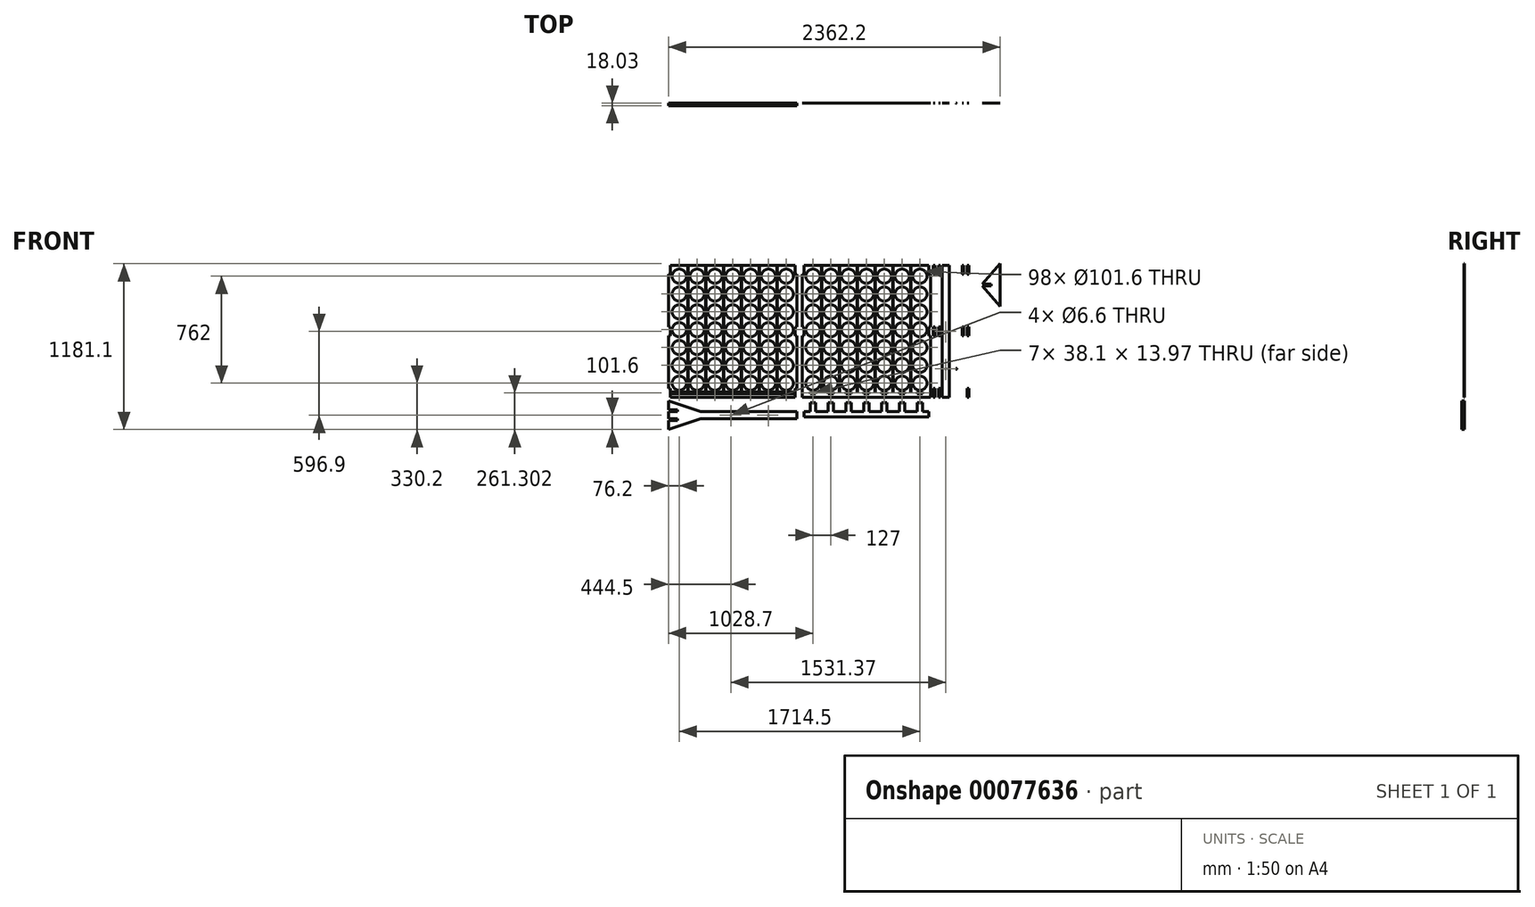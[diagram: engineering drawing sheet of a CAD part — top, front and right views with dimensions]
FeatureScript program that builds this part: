
annotation { "Feature Type Name" : "Feature", "Feature Type Description" : "" }
export const myFeature = defineFeature(function(context is Context, id is Id, definition is map)
    precondition{}
    {
        {
            assignVariable(context, id + "F0", {"name" : "Thickness", "anyValue" : .48});
        }
        {
            var Q0;
            Q0=qCreatedBy(makeId("Front.planeOp"),FACE);
            var sketch = newSketch(context, id + "F1", { "sketchPlane" : qUnion([Q0])});
            skLineSegment(sketch, "E0.bottom", {"start": v(-1219.2, 609.6) * mm, "end": v(1219.2, 609.6) * mm});
            skLineSegment(sketch, "E0.top", {"start": v(-1219.2, -609.6) * mm, "end": v(1219.2, -609.6) * mm});
            skLineSegment(sketch, "E0.left", {"start": v(-1219.2, 609.6) * mm, "end": v(-1219.2, -609.6) * mm});
            skLineSegment(sketch, "E0.right", {"start": v(1219.2, 609.6) * mm, "end": v(1219.2, -609.6) * mm});
            skPoint(sketch, "E0.middle", {"position": v(0, 0) * mm});
            skLineSegment(sketch, "E1.bottom", {"start": v(-1181.1, 571.5) * mm, "end": v(-266.7, 571.5) * mm});
            skLineSegment(sketch, "E1.top", {"start": v(-1181.1, -368.3) * mm, "end": v(-266.7, -368.3) * mm});
            skLineSegment(sketch, "E1.left", {"start": v(-1181.1, 571.5) * mm, "end": v(-1181.1, -368.3) * mm});
            skLineSegment(sketch, "E1.right", {"start": v(-266.7, 571.5) * mm, "end": v(-266.7, -368.3) * mm});
            skLineSegment(sketch, "E2.bottom", {"start": v(-228.6, 571.5) * mm, "end": v(685.8, 571.5) * mm});
            skLineSegment(sketch, "E2.top", {"start": v(-228.6, -368.3) * mm, "end": v(685.8, -368.3) * mm});
            skLineSegment(sketch, "E2.left", {"start": v(-228.6, 571.5) * mm, "end": v(-228.6, -368.3) * mm});
            skLineSegment(sketch, "E2.right", {"start": v(685.8, 571.5) * mm, "end": v(685.8, -368.3) * mm});
            skCircle(sketch, "E3", {"center": v(-1104.9, 495.3) * mm, "radius": 50.8 * mm});
            skCircle(sketch, "E4.0.1.0", {"center": v(-1104.9, 368.3) * mm, "radius": 50.8 * mm});
            skCircle(sketch, "E4.0.2.0", {"center": v(-1104.9, 241.3) * mm, "radius": 50.8 * mm});
            skCircle(sketch, "E4.0.3.0", {"center": v(-1104.9, 114.3) * mm, "radius": 50.8 * mm});
            skCircle(sketch, "E4.0.4.0", {"center": v(-1104.9, -12.7) * mm, "radius": 50.8 * mm});
            skCircle(sketch, "E4.0.5.0", {"center": v(-1104.9, -139.7) * mm, "radius": 50.8 * mm});
            skCircle(sketch, "E4.1.0.0", {"center": v(-977.9, 495.3) * mm, "radius": 50.8 * mm});
            skCircle(sketch, "E4.1.1.0", {"center": v(-977.9, 368.3) * mm, "radius": 50.8 * mm});
            skCircle(sketch, "E4.1.2.0", {"center": v(-977.9, 241.3) * mm, "radius": 50.8 * mm});
            skCircle(sketch, "E4.1.3.0", {"center": v(-977.9, 114.3) * mm, "radius": 50.8 * mm});
            skCircle(sketch, "E4.1.4.0", {"center": v(-977.9, -12.7) * mm, "radius": 50.8 * mm});
            skCircle(sketch, "E4.1.5.0", {"center": v(-977.9, -139.7) * mm, "radius": 50.8 * mm});
            skCircle(sketch, "E4.2.0.0", {"center": v(-850.9, 495.3) * mm, "radius": 50.8 * mm});
            skCircle(sketch, "E4.2.1.0", {"center": v(-850.9, 368.3) * mm, "radius": 50.8 * mm});
            skCircle(sketch, "E4.2.2.0", {"center": v(-850.9, 241.3) * mm, "radius": 50.8 * mm});
            skCircle(sketch, "E4.2.3.0", {"center": v(-850.9, 114.3) * mm, "radius": 50.8 * mm});
            skCircle(sketch, "E4.2.4.0", {"center": v(-850.9, -12.7) * mm, "radius": 50.8 * mm});
            skCircle(sketch, "E4.2.5.0", {"center": v(-850.9, -139.7) * mm, "radius": 50.8 * mm});
            skCircle(sketch, "E4.3.0.0", {"center": v(-723.9, 495.3) * mm, "radius": 50.8 * mm});
            skCircle(sketch, "E4.3.1.0", {"center": v(-723.9, 368.3) * mm, "radius": 50.8 * mm});
            skCircle(sketch, "E4.3.2.0", {"center": v(-723.9, 241.3) * mm, "radius": 50.8 * mm});
            skCircle(sketch, "E4.3.3.0", {"center": v(-723.9, 114.3) * mm, "radius": 50.8 * mm});
            skCircle(sketch, "E4.3.4.0", {"center": v(-723.9, -12.7) * mm, "radius": 50.8 * mm});
            skCircle(sketch, "E4.3.5.0", {"center": v(-723.9, -139.7) * mm, "radius": 50.8 * mm});
            skCircle(sketch, "E4.4.0.0", {"center": v(-596.9, 495.3) * mm, "radius": 50.8 * mm});
            skCircle(sketch, "E4.4.1.0", {"center": v(-596.9, 368.3) * mm, "radius": 50.8 * mm});
            skCircle(sketch, "E4.4.2.0", {"center": v(-596.9, 241.3) * mm, "radius": 50.8 * mm});
            skCircle(sketch, "E4.4.3.0", {"center": v(-596.9, 114.3) * mm, "radius": 50.8 * mm});
            skCircle(sketch, "E4.4.4.0", {"center": v(-596.9, -12.7) * mm, "radius": 50.8 * mm});
            skCircle(sketch, "E4.4.5.0", {"center": v(-596.9, -139.7) * mm, "radius": 50.8 * mm});
            skCircle(sketch, "E4.5.0.0", {"center": v(-469.9, 495.3) * mm, "radius": 50.8 * mm});
            skCircle(sketch, "E4.5.1.0", {"center": v(-469.9, 368.3) * mm, "radius": 50.8 * mm});
            skCircle(sketch, "E4.5.2.0", {"center": v(-469.9, 241.3) * mm, "radius": 50.8 * mm});
            skCircle(sketch, "E4.5.3.0", {"center": v(-469.9, 114.3) * mm, "radius": 50.8 * mm});
            skCircle(sketch, "E4.5.4.0", {"center": v(-469.9, -12.7) * mm, "radius": 50.8 * mm});
            skCircle(sketch, "E4.5.5.0", {"center": v(-469.9, -139.7) * mm, "radius": 50.8 * mm});
            skLineSegment(sketch, "E4.direction1", {"start": v(-1104.9, 495.3) * mm, "end": v(-977.9, 495.3) * mm, "construction": true});
            skLineSegment(sketch, "E4.direction2", {"start": v(-1104.9, 495.3) * mm, "end": v(-1104.9, 368.3) * mm, "construction": true});
            skCircle(sketch, "E5", {"center": v(-152.4, 495.3) * mm, "radius": 50.8 * mm});
            skCircle(sketch, "E6.0.1.0", {"center": v(-152.4, 368.3) * mm, "radius": 50.8 * mm});
            skCircle(sketch, "E6.0.2.0", {"center": v(-152.4, 241.3) * mm, "radius": 50.8 * mm});
            skCircle(sketch, "E6.0.3.0", {"center": v(-152.4, 114.3) * mm, "radius": 50.8 * mm});
            skCircle(sketch, "E6.0.4.0", {"center": v(-152.4, -12.7) * mm, "radius": 50.8 * mm});
            skCircle(sketch, "E6.0.5.0", {"center": v(-152.4, -139.7) * mm, "radius": 50.8 * mm});
            skCircle(sketch, "E6.1.0.0", {"center": v(-25.4, 495.3) * mm, "radius": 50.8 * mm});
            skCircle(sketch, "E6.1.1.0", {"center": v(-25.4, 368.3) * mm, "radius": 50.8 * mm});
            skCircle(sketch, "E6.1.2.0", {"center": v(-25.4, 241.3) * mm, "radius": 50.8 * mm});
            skCircle(sketch, "E6.1.3.0", {"center": v(-25.4, 114.3) * mm, "radius": 50.8 * mm});
            skCircle(sketch, "E6.1.4.0", {"center": v(-25.4, -12.7) * mm, "radius": 50.8 * mm});
            skCircle(sketch, "E6.1.5.0", {"center": v(-25.4, -139.7) * mm, "radius": 50.8 * mm});
            skCircle(sketch, "E6.2.0.0", {"center": v(101.6, 495.3) * mm, "radius": 50.8 * mm});
            skCircle(sketch, "E6.2.1.0", {"center": v(101.6, 368.3) * mm, "radius": 50.8 * mm});
            skCircle(sketch, "E6.2.2.0", {"center": v(101.6, 241.3) * mm, "radius": 50.8 * mm});
            skCircle(sketch, "E6.2.3.0", {"center": v(101.6, 114.3) * mm, "radius": 50.8 * mm});
            skCircle(sketch, "E6.2.4.0", {"center": v(101.6, -12.7) * mm, "radius": 50.8 * mm});
            skCircle(sketch, "E6.2.5.0", {"center": v(101.6, -139.7) * mm, "radius": 50.8 * mm});
            skCircle(sketch, "E6.3.0.0", {"center": v(228.6, 495.3) * mm, "radius": 50.8 * mm});
            skCircle(sketch, "E6.3.1.0", {"center": v(228.6, 368.3) * mm, "radius": 50.8 * mm});
            skCircle(sketch, "E6.3.2.0", {"center": v(228.6, 241.3) * mm, "radius": 50.8 * mm});
            skCircle(sketch, "E6.3.3.0", {"center": v(228.6, 114.3) * mm, "radius": 50.8 * mm});
            skCircle(sketch, "E6.3.4.0", {"center": v(228.6, -12.7) * mm, "radius": 50.8 * mm});
            skCircle(sketch, "E6.3.5.0", {"center": v(228.6, -139.7) * mm, "radius": 50.8 * mm});
            skCircle(sketch, "E6.4.0.0", {"center": v(355.6, 495.3) * mm, "radius": 50.8 * mm});
            skCircle(sketch, "E6.4.1.0", {"center": v(355.6, 368.3) * mm, "radius": 50.8 * mm});
            skCircle(sketch, "E6.4.2.0", {"center": v(355.6, 241.3) * mm, "radius": 50.8 * mm});
            skCircle(sketch, "E6.4.3.0", {"center": v(355.6, 114.3) * mm, "radius": 50.8 * mm});
            skCircle(sketch, "E6.4.4.0", {"center": v(355.6, -12.7) * mm, "radius": 50.8 * mm});
            skCircle(sketch, "E6.4.5.0", {"center": v(355.6, -139.7) * mm, "radius": 50.8 * mm});
            skCircle(sketch, "E6.5.0.0", {"center": v(482.6, 495.3) * mm, "radius": 50.8 * mm});
            skCircle(sketch, "E6.5.1.0", {"center": v(482.6, 368.3) * mm, "radius": 50.8 * mm});
            skCircle(sketch, "E6.5.2.0", {"center": v(482.6, 241.3) * mm, "radius": 50.8 * mm});
            skCircle(sketch, "E6.5.3.0", {"center": v(482.6, 114.3) * mm, "radius": 50.8 * mm});
            skCircle(sketch, "E6.5.4.0", {"center": v(482.6, -12.7) * mm, "radius": 50.8 * mm});
            skCircle(sketch, "E6.5.5.0", {"center": v(482.6, -139.7) * mm, "radius": 50.8 * mm});
            skLineSegment(sketch, "E6.direction1", {"start": v(-152.4, 495.3) * mm, "end": v(-25.4, 495.3) * mm, "construction": true});
            skLineSegment(sketch, "E6.direction2", {"start": v(-152.4, 495.3) * mm, "end": v(-152.4, 368.3) * mm, "construction": true});
            skLineSegment(sketch, "E7", {"start": v(-1041.4, 571.5) * mm, "end": v(-1041.4, -368.3) * mm, "construction": true});
            skPoint(sketch, "E7.startSnap0", {"position": v(-1041.4, 495.3) * mm});
            skLineSegment(sketch, "E8.0", {"start": v(-1042.99, 571.5) * mm, "end": v(-1042.99, -328.61) * mm});
            skLineSegment(sketch, "E9.0", {"start": v(-1039.81, 571.5) * mm, "end": v(-1039.81, -328.61) * mm});
            skLineSegment(sketch, "E10.1.0.0", {"start": v(-912.81, 571.5) * mm, "end": v(-912.81, -328.61) * mm});
            skLineSegment(sketch, "E10.1.0.1", {"start": v(-915.99, 571.5) * mm, "end": v(-915.99, -328.61) * mm});
            skLineSegment(sketch, "E10.2.0.0", {"start": v(-785.81, 571.5) * mm, "end": v(-785.81, -328.61) * mm});
            skLineSegment(sketch, "E10.2.0.1", {"start": v(-788.99, 571.5) * mm, "end": v(-788.99, -328.61) * mm});
            skLineSegment(sketch, "E10.3.0.0", {"start": v(-658.81, 571.5) * mm, "end": v(-658.81, -328.61) * mm});
            skLineSegment(sketch, "E10.3.0.1", {"start": v(-661.99, 571.5) * mm, "end": v(-661.99, -328.61) * mm});
            skLineSegment(sketch, "E10.4.0.0", {"start": v(-531.81, 571.5) * mm, "end": v(-531.81, -328.61) * mm});
            skLineSegment(sketch, "E10.4.0.1", {"start": v(-534.99, 571.5) * mm, "end": v(-534.99, -328.61) * mm});
            skLineSegment(sketch, "E10.direction1", {"start": v(-1039.81, -328.61) * mm, "end": v(-912.81, -328.61) * mm, "construction": true});
            skLineSegment(sketch, "E11", {"start": v(-88.9, 571.5) * mm, "end": v(-88.9, -368.3) * mm, "construction": true});
            skPoint(sketch, "E11.startSnap0", {"position": v(-88.9, 495.3) * mm});
            skLineSegment(sketch, "E12.0", {"start": v(-87.31, 571.5) * mm, "end": v(-87.31, -328.61) * mm});
            skLineSegment(sketch, "E13.0", {"start": v(-90.49, 571.5) * mm, "end": v(-90.49, -328.61) * mm});
            skLineSegment(sketch, "E14.1.0.0", {"start": v(39.69, 571.5) * mm, "end": v(39.69, -328.61) * mm});
            skLineSegment(sketch, "E14.1.0.1", {"start": v(36.51, 571.5) * mm, "end": v(36.51, -328.61) * mm});
            skLineSegment(sketch, "E14.2.0.0", {"start": v(166.69, 571.5) * mm, "end": v(166.69, -328.61) * mm});
            skLineSegment(sketch, "E14.2.0.1", {"start": v(163.51, 571.5) * mm, "end": v(163.51, -328.61) * mm});
            skLineSegment(sketch, "E14.3.0.0", {"start": v(293.69, 571.5) * mm, "end": v(293.69, -328.61) * mm});
            skLineSegment(sketch, "E14.3.0.1", {"start": v(290.51, 571.5) * mm, "end": v(290.51, -328.61) * mm});
            skLineSegment(sketch, "E14.4.0.0", {"start": v(420.69, 571.5) * mm, "end": v(420.69, -328.61) * mm});
            skLineSegment(sketch, "E14.4.0.1", {"start": v(417.51, 571.5) * mm, "end": v(417.51, -328.61) * mm});
            skLineSegment(sketch, "E14.direction1", {"start": v(-87.31, -328.61) * mm, "end": v(39.69, -328.61) * mm, "construction": true});
            skCircle(sketch, "E15.0.6.0", {"center": v(-342.9, 495.3) * mm, "radius": 50.8 * mm});
            skCircle(sketch, "E15.0.6.1", {"center": v(-342.9, 368.3) * mm, "radius": 50.8 * mm});
            skCircle(sketch, "E15.0.6.2", {"center": v(-342.9, 241.3) * mm, "radius": 50.8 * mm});
            skCircle(sketch, "E15.0.6.3", {"center": v(-342.9, 114.3) * mm, "radius": 50.8 * mm});
            skCircle(sketch, "E15.0.6.4", {"center": v(-342.9, -12.7) * mm, "radius": 50.8 * mm});
            skCircle(sketch, "E15.0.6.5", {"center": v(-342.9, -139.7) * mm, "radius": 50.8 * mm});
            skCircle(sketch, "E16.0.0.6", {"center": v(-1104.9, -266.7) * mm, "radius": 50.8 * mm});
            skCircle(sketch, "E16.0.1.6", {"center": v(-977.9, -266.7) * mm, "radius": 50.8 * mm});
            skCircle(sketch, "E16.0.2.6", {"center": v(-850.9, -266.7) * mm, "radius": 50.8 * mm});
            skCircle(sketch, "E16.0.3.6", {"center": v(-723.9, -266.7) * mm, "radius": 50.8 * mm});
            skCircle(sketch, "E16.0.4.6", {"center": v(-596.9, -266.7) * mm, "radius": 50.8 * mm});
            skCircle(sketch, "E16.0.5.6", {"center": v(-469.9, -266.7) * mm, "radius": 50.8 * mm});
            skCircle(sketch, "E16.0.6.6", {"center": v(-342.9, -266.7) * mm, "radius": 50.8 * mm});
            skLineSegment(sketch, "E17.0.5.0", {"start": v(-404.81, 571.5) * mm, "end": v(-404.81, -328.61) * mm});
            skLineSegment(sketch, "E17.3.5.0", {"start": v(-407.99, 571.5) * mm, "end": v(-407.99, -328.61) * mm});
            skLineSegment(sketch, "E18.0.5.0", {"start": v(547.69, 571.5) * mm, "end": v(547.69, -328.61) * mm});
            skLineSegment(sketch, "E18.3.5.0", {"start": v(544.51, 571.5) * mm, "end": v(544.51, -328.61) * mm});
            skCircle(sketch, "E19.0.6.0", {"center": v(609.6, 495.3) * mm, "radius": 50.8 * mm});
            skCircle(sketch, "E19.0.6.1", {"center": v(609.6, 368.3) * mm, "radius": 50.8 * mm});
            skCircle(sketch, "E19.0.6.2", {"center": v(609.6, 241.3) * mm, "radius": 50.8 * mm});
            skCircle(sketch, "E19.0.6.3", {"center": v(609.6, 114.3) * mm, "radius": 50.8 * mm});
            skCircle(sketch, "E19.0.6.4", {"center": v(609.6, -12.7) * mm, "radius": 50.8 * mm});
            skCircle(sketch, "E19.0.6.5", {"center": v(609.6, -139.7) * mm, "radius": 50.8 * mm});
            skCircle(sketch, "E20.0.0.6", {"center": v(-152.4, -266.7) * mm, "radius": 50.8 * mm});
            skCircle(sketch, "E20.0.1.6", {"center": v(-25.4, -266.7) * mm, "radius": 50.8 * mm});
            skCircle(sketch, "E20.0.2.6", {"center": v(101.6, -266.7) * mm, "radius": 50.8 * mm});
            skCircle(sketch, "E20.0.3.6", {"center": v(228.6, -266.7) * mm, "radius": 50.8 * mm});
            skCircle(sketch, "E20.0.4.6", {"center": v(355.6, -266.7) * mm, "radius": 50.8 * mm});
            skCircle(sketch, "E20.0.5.6", {"center": v(482.6, -266.7) * mm, "radius": 50.8 * mm});
            skCircle(sketch, "E20.0.6.6", {"center": v(609.6, -266.7) * mm, "radius": 50.8 * mm});
            skLineSegment(sketch, "E21", {"start": v(-1042.99, -328.61) * mm, "end": v(-1039.81, -328.61) * mm});
            skLineSegment(sketch, "E22.1.0.0", {"start": v(-915.99, -328.61) * mm, "end": v(-912.81, -328.61) * mm});
            skLineSegment(sketch, "E22.2.0.0", {"start": v(-788.99, -328.61) * mm, "end": v(-785.81, -328.61) * mm});
            skLineSegment(sketch, "E22.3.0.0", {"start": v(-661.99, -328.61) * mm, "end": v(-658.81, -328.61) * mm});
            skLineSegment(sketch, "E22.4.0.0", {"start": v(-534.99, -328.61) * mm, "end": v(-531.81, -328.61) * mm});
            skLineSegment(sketch, "E22.5.0.0", {"start": v(-407.99, -328.61) * mm, "end": v(-404.81, -328.61) * mm});
            skLineSegment(sketch, "E22.direction1", {"start": v(-1042.99, -328.61) * mm, "end": v(-915.99, -328.61) * mm, "construction": true});
            skLineSegment(sketch, "E23", {"start": v(-90.49, -328.61) * mm, "end": v(-87.31, -328.61) * mm});
            skLineSegment(sketch, "E24.1.0.0", {"start": v(36.51, -328.61) * mm, "end": v(39.69, -328.61) * mm});
            skLineSegment(sketch, "E24.2.0.0", {"start": v(163.51, -328.61) * mm, "end": v(166.69, -328.61) * mm});
            skLineSegment(sketch, "E24.3.0.0", {"start": v(290.51, -328.61) * mm, "end": v(293.69, -328.61) * mm});
            skLineSegment(sketch, "E24.4.0.0", {"start": v(417.51, -328.61) * mm, "end": v(420.69, -328.61) * mm});
            skLineSegment(sketch, "E24.5.0.0", {"start": v(544.51, -328.61) * mm, "end": v(547.69, -328.61) * mm});
            skLineSegment(sketch, "E24.direction1", {"start": v(-90.49, -328.61) * mm, "end": v(36.51, -328.61) * mm, "construction": true});
            skLineSegment(sketch, "E25.bottom", {"start": v(-1181.1, 571.5) * mm, "end": v(-1168.9, 571.5) * mm});
            skLineSegment(sketch, "E25.top", {"start": v(-1181.1, -368.3) * mm, "end": v(-1168.9, -368.3) * mm});
            skLineSegment(sketch, "E25.right", {"start": v(-1168.9, 571.5) * mm, "end": v(-1168.9, -368.3) * mm, "construction": true});
            skLineSegment(sketch, "E26.0", {"start": v(-278.9, 571.5) * mm, "end": v(-278.9, -368.3) * mm, "construction": true});
            skLineSegment(sketch, "E27.0", {"start": v(-216.4, 571.5) * mm, "end": v(-216.4, -368.3) * mm, "construction": true});
            skLineSegment(sketch, "E28.0", {"start": v(673.6, 571.5) * mm, "end": v(673.6, -368.3) * mm, "construction": true});
            skCircle(sketch, "E29", {"center": v(-977.9, -266.7) * mm, "radius": 61.91 * mm, "construction": true});
            skLineSegment(sketch, "E30", {"start": v(-1168.9, -328.61) * mm, "end": v(-278.9, -328.61) * mm});
            skLineSegment(sketch, "E31.0", {"start": v(-1168.9, -342.58) * mm, "end": v(-278.9, -342.58) * mm});
            skLineSegment(sketch, "E32", {"start": v(-216.4, -328.61) * mm, "end": v(673.6, -328.61) * mm, "construction": true});
            skLineSegment(sketch, "E33.0", {"start": v(-216.4, -342.58) * mm, "end": v(673.6, -342.58) * mm, "construction": true});
            skLineSegment(sketch, "E34.top", {"start": v(-1181.1, -304.8) * mm, "end": v(-1168.9, -304.8) * mm});
            skLineSegment(sketch, "E34.left", {"start": v(-1181.1, -368.3) * mm, "end": v(-1181.1, -304.8) * mm});
            skLineSegment(sketch, "E34.right", {"start": v(-1168.9, -368.3) * mm, "end": v(-1168.9, -304.8) * mm});
            skLineSegment(sketch, "E35.top", {"start": v(-1181.1, 508) * mm, "end": v(-1168.9, 508) * mm});
            skLineSegment(sketch, "E35.left", {"start": v(-1181.1, 571.5) * mm, "end": v(-1181.1, 508) * mm});
            skLineSegment(sketch, "E35.right", {"start": v(-1168.9, 571.5) * mm, "end": v(-1168.9, 508) * mm});
            skLineSegment(sketch, "E36.bottom", {"start": v(-266.7, 571.5) * mm, "end": v(-278.9, 571.5) * mm});
            skLineSegment(sketch, "E36.top", {"start": v(-266.7, 508) * mm, "end": v(-278.9, 508) * mm});
            skLineSegment(sketch, "E36.left", {"start": v(-266.7, 571.5) * mm, "end": v(-266.7, 508) * mm});
            skLineSegment(sketch, "E36.right", {"start": v(-278.9, 571.5) * mm, "end": v(-278.9, 508) * mm});
            skLineSegment(sketch, "E37.bottom", {"start": v(-228.6, 571.5) * mm, "end": v(-216.4, 571.5) * mm});
            skLineSegment(sketch, "E37.top", {"start": v(-228.6, 508) * mm, "end": v(-216.4, 508) * mm});
            skLineSegment(sketch, "E37.left", {"start": v(-228.6, 571.5) * mm, "end": v(-228.6, 508) * mm});
            skLineSegment(sketch, "E37.right", {"start": v(-216.4, 571.5) * mm, "end": v(-216.4, 508) * mm});
            skLineSegment(sketch, "E38.bottom", {"start": v(-266.7, -368.3) * mm, "end": v(-278.9, -368.3) * mm});
            skLineSegment(sketch, "E38.top", {"start": v(-266.7, -304.8) * mm, "end": v(-278.9, -304.8) * mm});
            skLineSegment(sketch, "E38.left", {"start": v(-266.7, -368.3) * mm, "end": v(-266.7, -304.8) * mm});
            skLineSegment(sketch, "E38.right", {"start": v(-278.9, -368.3) * mm, "end": v(-278.9, -304.8) * mm});
            skLineSegment(sketch, "E39.bottom", {"start": v(-228.6, -368.3) * mm, "end": v(-216.4, -368.3) * mm});
            skLineSegment(sketch, "E39.top", {"start": v(-228.6, -304.8) * mm, "end": v(-216.4, -304.8) * mm});
            skLineSegment(sketch, "E39.left", {"start": v(-228.6, -368.3) * mm, "end": v(-228.6, -304.8) * mm});
            skLineSegment(sketch, "E39.right", {"start": v(-216.4, -368.3) * mm, "end": v(-216.4, -304.8) * mm});
            skLineSegment(sketch, "E40.bottom", {"start": v(685.8, -368.3) * mm, "end": v(673.6, -368.3) * mm});
            skLineSegment(sketch, "E40.top", {"start": v(685.8, -304.8) * mm, "end": v(673.6, -304.8) * mm});
            skLineSegment(sketch, "E40.left", {"start": v(685.8, -368.3) * mm, "end": v(685.8, -304.8) * mm});
            skLineSegment(sketch, "E40.right", {"start": v(673.6, -368.3) * mm, "end": v(673.6, -304.8) * mm});
            skLineSegment(sketch, "E41.bottom", {"start": v(685.8, 571.5) * mm, "end": v(673.6, 571.5) * mm});
            skLineSegment(sketch, "E41.top", {"start": v(685.8, 508) * mm, "end": v(673.6, 508) * mm});
            skLineSegment(sketch, "E41.left", {"start": v(685.8, 571.5) * mm, "end": v(685.8, 508) * mm});
            skLineSegment(sketch, "E41.right", {"start": v(673.6, 571.5) * mm, "end": v(673.6, 508) * mm});
            skLineSegment(sketch, "E42.bottom", {"start": v(-1181.1, 133.35) * mm, "end": v(-1168.9, 133.35) * mm});
            skLineSegment(sketch, "E42.top", {"start": v(-1181.1, 69.85) * mm, "end": v(-1168.9, 69.85) * mm});
            skLineSegment(sketch, "E42.left", {"start": v(-1181.1, 133.35) * mm, "end": v(-1181.1, 69.85) * mm});
            skLineSegment(sketch, "E42.right", {"start": v(-1168.9, 133.35) * mm, "end": v(-1168.9, 69.85) * mm});
            skPoint(sketch, "E43", {"position": v(-1181.1, 101.6) * mm});
            skLineSegment(sketch, "E44", {"start": v(-723.9, 571.5) * mm, "end": v(-723.9, -368.3) * mm, "construction": true});
            skLineSegment(sketch, "E45", {"start": v(228.6, 571.5) * mm, "end": v(228.6, -368.3) * mm, "construction": true});
            skLineSegment(sketch, "E46.MirrorCS", {"start": v(-266.7, 69.85) * mm, "end": v(-278.9, 69.85) * mm});
            skLineSegment(sketch, "E47.MirrorCS", {"start": v(-266.7, 133.35) * mm, "end": v(-278.9, 133.35) * mm});
            skPoint(sketch, "E48.MirrorP", {"position": v(-266.7, 101.6) * mm});
            skLineSegment(sketch, "E49.MirrorCS", {"start": v(-266.7, 133.35) * mm, "end": v(-266.7, 69.85) * mm});
            skLineSegment(sketch, "E50.MirrorCS", {"start": v(-278.9, 133.35) * mm, "end": v(-278.9, 69.85) * mm});
            skLineSegment(sketch, "E51", {"start": v(-266.7, 101.6) * mm, "end": v(-228.6, 101.6) * mm, "construction": true});
            skLineSegment(sketch, "E52", {"start": v(-228.6, 101.6) * mm, "end": v(-247.65, 69.85) * mm, "construction": true});
            skPoint(sketch, "E52.endSnap0", {"position": v(-247.65, 101.6) * mm});
            skLineSegment(sketch, "E53", {"start": v(-247.65, 69.85) * mm, "end": v(-247.65, 101.6) * mm, "construction": true});
            skPoint(sketch, "E54.MirrorP", {"position": v(-228.6, 101.6) * mm});
            skLineSegment(sketch, "E55.MirrorCS", {"start": v(-216.4, 133.35) * mm, "end": v(-216.4, 69.85) * mm});
            skLineSegment(sketch, "E56.MirrorCS", {"start": v(-228.6, 133.35) * mm, "end": v(-228.6, 69.85) * mm});
            skLineSegment(sketch, "E57.MirrorCS", {"start": v(-228.6, 69.85) * mm, "end": v(-216.4, 69.85) * mm});
            skLineSegment(sketch, "E58.MirrorCS", {"start": v(-228.6, 133.35) * mm, "end": v(-216.4, 133.35) * mm});
            skPoint(sketch, "E59.MirrorP", {"position": v(685.8, 101.6) * mm});
            skLineSegment(sketch, "E60.MirrorCS", {"start": v(673.6, 133.35) * mm, "end": v(673.6, 69.85) * mm});
            skLineSegment(sketch, "E61.MirrorCS", {"start": v(685.8, 133.35) * mm, "end": v(685.8, 69.85) * mm});
            skLineSegment(sketch, "E62.MirrorCS", {"start": v(685.8, 133.35) * mm, "end": v(673.6, 133.35) * mm});
            skLineSegment(sketch, "E63.MirrorCS", {"start": v(685.8, 69.85) * mm, "end": v(673.6, 69.85) * mm});
            skLineSegment(sketch, "E64.bottom", {"start": v(704.85, 571.5) * mm, "end": v(754.63, 571.5) * mm});
            skLineSegment(sketch, "E64.top", {"start": v(704.85, -368.3) * mm, "end": v(754.63, -368.3) * mm});
            skLineSegment(sketch, "E65.bottom", {"start": v(704.85, -368.3) * mm, "end": v(717.04, -368.3) * mm});
            skLineSegment(sketch, "E65.top", {"start": v(704.85, -304.8) * mm, "end": v(717.04, -304.8) * mm});
            skLineSegment(sketch, "E65.left", {"start": v(704.85, -368.3) * mm, "end": v(704.85, -304.8) * mm});
            skLineSegment(sketch, "E65.right", {"start": v(717.04, -368.3) * mm, "end": v(717.04, -304.8) * mm});
            skLineSegment(sketch, "E66.bottom", {"start": v(754.63, -368.3) * mm, "end": v(742.44, -368.3) * mm});
            skLineSegment(sketch, "E66.top", {"start": v(754.63, -304.8) * mm, "end": v(742.44, -304.8) * mm});
            skLineSegment(sketch, "E66.left", {"start": v(754.63, -368.3) * mm, "end": v(754.63, -304.8) * mm});
            skLineSegment(sketch, "E66.right", {"start": v(742.44, -368.3) * mm, "end": v(742.44, -304.8) * mm});
            skLineSegment(sketch, "E67.bottom", {"start": v(704.85, 571.5) * mm, "end": v(717.04, 571.5) * mm});
            skLineSegment(sketch, "E67.top", {"start": v(704.85, 508) * mm, "end": v(717.04, 508) * mm});
            skLineSegment(sketch, "E67.left", {"start": v(704.85, 571.5) * mm, "end": v(704.85, 508) * mm});
            skLineSegment(sketch, "E67.right", {"start": v(717.04, 571.5) * mm, "end": v(717.04, 508) * mm});
            skLineSegment(sketch, "E68.bottom", {"start": v(754.63, 571.5) * mm, "end": v(742.44, 571.5) * mm});
            skLineSegment(sketch, "E68.top", {"start": v(754.63, 508) * mm, "end": v(742.44, 508) * mm});
            skLineSegment(sketch, "E68.left", {"start": v(754.63, 571.5) * mm, "end": v(754.63, 508) * mm});
            skLineSegment(sketch, "E68.right", {"start": v(742.44, 571.5) * mm, "end": v(742.44, 508) * mm});
            skLineSegment(sketch, "E69", {"start": v(717.04, 508) * mm, "end": v(717.04, -304.8) * mm});
            skLineSegment(sketch, "E70", {"start": v(742.44, -304.8) * mm, "end": v(742.44, 508) * mm});
            skLineSegment(sketch, "E71.bottom", {"start": v(717.04, 133.35) * mm, "end": v(704.85, 133.35) * mm});
            skLineSegment(sketch, "E71.top", {"start": v(717.04, 69.85) * mm, "end": v(704.85, 69.85) * mm});
            skLineSegment(sketch, "E71.left", {"start": v(717.04, 133.35) * mm, "end": v(717.04, 69.85) * mm});
            skLineSegment(sketch, "E71.right", {"start": v(704.85, 133.35) * mm, "end": v(704.85, 69.85) * mm});
            skLineSegment(sketch, "E72.bottom", {"start": v(742.44, 133.35) * mm, "end": v(754.63, 133.35) * mm});
            skLineSegment(sketch, "E72.top", {"start": v(742.44, 69.85) * mm, "end": v(754.63, 69.85) * mm});
            skLineSegment(sketch, "E72.left", {"start": v(742.44, 133.35) * mm, "end": v(742.44, 69.85) * mm});
            skLineSegment(sketch, "E72.right", {"start": v(754.63, 133.35) * mm, "end": v(754.63, 69.85) * mm});
            skLineSegment(sketch, "E73.bottom", {"start": v(769.87, 571.5) * mm, "end": v(819.66, 571.5) * mm});
            skLineSegment(sketch, "E73.top", {"start": v(769.87, -368.3) * mm, "end": v(819.66, -368.3) * mm});
            skLineSegment(sketch, "E73.left", {"start": v(769.87, 571.5) * mm, "end": v(769.87, -368.3) * mm});
            skLineSegment(sketch, "E73.right", {"start": v(819.66, 571.5) * mm, "end": v(819.66, -368.3) * mm});
            skCircle(sketch, "E74", {"center": v(729.74, 101.6) * mm, "radius": 3.3 * mm});
            skPoint(sketch, "E74.centerSnap0", {"position": v(742.44, 101.6) * mm});
            skPoint(sketch, "E74.centerSnap1", {"position": v(729.74, 571.5) * mm});
            skCircle(sketch, "E75", {"center": v(794.77, 101.6) * mm, "radius": 3.3 * mm});
            skPoint(sketch, "E75.centerSnap0", {"position": v(769.87, 101.6) * mm});
            skPoint(sketch, "E75.centerSnap1", {"position": v(794.77, 571.5) * mm});
            skCircle(sketch, "E76", {"center": v(729.74, -165.1) * mm, "radius": 3.3 * mm});
            skCircle(sketch, "E77", {"center": v(794.77, -165.1) * mm, "radius": 3.3 * mm});
            skPoint(sketch, "E77.centerSnap0", {"position": v(794.77, -368.3) * mm});
            skLineSegment(sketch, "E78", {"start": v(832.36, 571.5) * mm, "end": v(832.36, -368.3) * mm, "construction": true});
            skLineSegment(sketch, "E79.MirrorCS", {"start": v(959.87, 571.5) * mm, "end": v(910.08, 571.5) * mm});
            skLineSegment(sketch, "E80.MirrorCS", {"start": v(959.87, -368.3) * mm, "end": v(947.67, -368.3) * mm});
            skLineSegment(sketch, "E81.MirrorCS", {"start": v(959.87, 571.5) * mm, "end": v(947.67, 571.5) * mm});
            skLineSegment(sketch, "E82.MirrorCS", {"start": v(959.87, -368.3) * mm, "end": v(910.08, -368.3) * mm});
            skLineSegment(sketch, "E83.MirrorCS", {"start": v(910.08, 571.5) * mm, "end": v(922.27, 571.5) * mm});
            skLineSegment(sketch, "E84.MirrorCS", {"start": v(947.67, 69.85) * mm, "end": v(959.87, 69.85) * mm});
            skLineSegment(sketch, "E85.MirrorCS", {"start": v(910.08, -368.3) * mm, "end": v(922.27, -368.3) * mm});
            skLineSegment(sketch, "E86.MirrorCS", {"start": v(910.08, -304.8) * mm, "end": v(922.27, -304.8) * mm});
            skLineSegment(sketch, "E87.MirrorCS", {"start": v(959.87, -304.8) * mm, "end": v(947.67, -304.8) * mm});
            skLineSegment(sketch, "E88.MirrorCS", {"start": v(910.08, 508) * mm, "end": v(922.27, 508) * mm});
            skLineSegment(sketch, "E89.MirrorCS", {"start": v(922.27, 133.35) * mm, "end": v(910.08, 133.35) * mm});
            skLineSegment(sketch, "E90.MirrorCS", {"start": v(959.87, 508) * mm, "end": v(947.67, 508) * mm});
            skLineSegment(sketch, "E91.MirrorCS", {"start": v(922.27, 69.85) * mm, "end": v(910.08, 69.85) * mm});
            skLineSegment(sketch, "E92.MirrorCS", {"start": v(947.67, 133.35) * mm, "end": v(959.87, 133.35) * mm});
            skLineSegment(sketch, "E93.MirrorCS", {"start": v(947.67, -368.3) * mm, "end": v(947.67, -304.8) * mm});
            skLineSegment(sketch, "E94.MirrorCS", {"start": v(922.27, -368.3) * mm, "end": v(922.27, -304.8) * mm});
            skLineSegment(sketch, "E95.MirrorCS", {"start": v(947.67, 133.35) * mm, "end": v(947.67, 69.85) * mm});
            skLineSegment(sketch, "E96.MirrorCS", {"start": v(959.87, -368.3) * mm, "end": v(959.87, -304.8) * mm});
            skCircle(sketch, "E97.MirrorC", {"center": v(934.97, 101.6) * mm, "radius": 3.3 * mm});
            skCircle(sketch, "E98.MirrorC", {"center": v(869.95, -165.1) * mm, "radius": 3.3 * mm});
            skCircle(sketch, "E99.MirrorC", {"center": v(934.97, -165.1) * mm, "radius": 3.3 * mm});
            skLineSegment(sketch, "E100.MirrorCS", {"start": v(894.84, -368.3) * mm, "end": v(845.06, -368.3) * mm});
            skLineSegment(sketch, "E101.MirrorCS", {"start": v(910.08, -368.3) * mm, "end": v(910.08, -304.8) * mm});
            skLineSegment(sketch, "E102.MirrorCS", {"start": v(922.27, 133.35) * mm, "end": v(922.27, 69.85) * mm});
            skLineSegment(sketch, "E103.MirrorCS", {"start": v(894.84, 571.5) * mm, "end": v(845.06, 571.5) * mm});
            skCircle(sketch, "E104.MirrorC", {"center": v(869.95, 101.6) * mm, "radius": 3.3 * mm});
            skLineSegment(sketch, "E105.MirrorCS", {"start": v(910.08, 133.35) * mm, "end": v(910.08, 69.85) * mm});
            skPoint(sketch, "E106.MirrorP", {"position": v(934.97, 571.5) * mm});
            skPoint(sketch, "E107.MirrorP", {"position": v(922.27, 101.6) * mm});
            skLineSegment(sketch, "E108.MirrorCS", {"start": v(959.87, 133.35) * mm, "end": v(959.87, 69.85) * mm});
            skLineSegment(sketch, "E109.MirrorCS", {"start": v(910.08, 571.5) * mm, "end": v(910.08, 508) * mm});
            skLineSegment(sketch, "E110.MirrorCS", {"start": v(922.27, -304.8) * mm, "end": v(922.27, 508) * mm});
            skLineSegment(sketch, "E111.MirrorCS", {"start": v(947.67, 508) * mm, "end": v(947.67, -304.8) * mm});
            skLineSegment(sketch, "E112.MirrorCS", {"start": v(947.67, 571.5) * mm, "end": v(947.67, 508) * mm});
            skPoint(sketch, "E113.MirrorP", {"position": v(869.95, 571.5) * mm});
            skLineSegment(sketch, "E114.MirrorCS", {"start": v(845.06, 571.5) * mm, "end": v(845.06, -368.3) * mm});
            skPoint(sketch, "E115.MirrorP", {"position": v(869.95, -368.3) * mm});
            skLineSegment(sketch, "E116.MirrorCS", {"start": v(959.87, 571.5) * mm, "end": v(959.87, 508) * mm});
            skPoint(sketch, "E117.MirrorP", {"position": v(894.84, 101.6) * mm});
            skLineSegment(sketch, "E118.MirrorCS", {"start": v(922.27, 571.5) * mm, "end": v(922.27, 508) * mm});
            skLineSegment(sketch, "E119.MirrorCS", {"start": v(894.84, 571.5) * mm, "end": v(894.84, -368.3) * mm});
            skLineSegment(sketch, "E120.bottom", {"start": v(704.34, -328.61) * mm, "end": v(755.14, -328.61) * mm, "construction": true});
            skLineSegment(sketch, "E120.top", {"start": v(704.34, -342.58) * mm, "end": v(755.14, -342.58) * mm, "construction": true});
            skLineSegment(sketch, "E120.left", {"start": v(704.34, -328.61) * mm, "end": v(704.34, -342.58) * mm, "construction": true});
            skLineSegment(sketch, "E120.right", {"start": v(755.14, -328.61) * mm, "end": v(755.14, -342.58) * mm, "construction": true});
            skPoint(sketch, "E120.middle", {"position": v(729.74, -335.6) * mm});
            skPoint(sketch, "E120.middle.positionSnap0", {"position": v(729.74, -368.3) * mm});
            skPoint(sketch, "E120.centerSnap0", {"position": v(729.74, -368.3) * mm});
            skLineSegment(sketch, "E121.bottom", {"start": v(769.37, -328.61) * mm, "end": v(820.17, -328.61) * mm, "construction": true});
            skLineSegment(sketch, "E121.top", {"start": v(769.37, -342.58) * mm, "end": v(820.17, -342.58) * mm, "construction": true});
            skLineSegment(sketch, "E121.left", {"start": v(769.37, -328.61) * mm, "end": v(769.37, -342.58) * mm, "construction": true});
            skLineSegment(sketch, "E121.right", {"start": v(820.17, -328.61) * mm, "end": v(820.17, -342.58) * mm, "construction": true});
            skPoint(sketch, "E121.middle", {"position": v(794.77, -335.6) * mm});
            skLineSegment(sketch, "E122.MirrorCS", {"start": v(895.35, -342.58) * mm, "end": v(844.55, -342.58) * mm, "construction": true});
            skLineSegment(sketch, "E123.MirrorCS", {"start": v(844.55, -328.61) * mm, "end": v(844.55, -342.58) * mm, "construction": true});
            skLineSegment(sketch, "E124.MirrorCS", {"start": v(895.35, -328.61) * mm, "end": v(844.55, -328.61) * mm, "construction": true});
            skLineSegment(sketch, "E125.MirrorCS", {"start": v(895.35, -328.61) * mm, "end": v(895.35, -342.58) * mm, "construction": true});
            skPoint(sketch, "E126.MirrorP", {"position": v(869.95, -335.6) * mm});
            skLineSegment(sketch, "E127.MirrorCS", {"start": v(960.37, -328.61) * mm, "end": v(960.37, -342.58) * mm, "construction": true});
            skPoint(sketch, "E128.MirrorP", {"position": v(934.97, -335.6) * mm});
            skLineSegment(sketch, "E129.MirrorCS", {"start": v(960.37, -342.58) * mm, "end": v(909.57, -342.58) * mm, "construction": true});
            skLineSegment(sketch, "E130.MirrorCS", {"start": v(960.37, -328.61) * mm, "end": v(909.57, -328.61) * mm, "construction": true});
            skLineSegment(sketch, "E131.MirrorCS", {"start": v(909.57, -328.61) * mm, "end": v(909.57, -342.58) * mm, "construction": true});
            skLineSegment(sketch, "E132.bottom", {"start": v(-216.4, -406.4) * mm, "end": v(673.6, -406.4) * mm, "construction": true});
            skLineSegment(sketch, "E132.top", {"start": v(-216.4, -469.9) * mm, "end": v(673.6, -469.9) * mm, "construction": true});
            skLineSegment(sketch, "E133", {"start": v(-216.4, -406.4) * mm, "end": v(-216.4, -469.9) * mm, "construction": true});
            skLineSegment(sketch, "E134", {"start": v(673.6, -406.4) * mm, "end": v(673.6, -469.9) * mm, "construction": true});
            skLineSegment(sketch, "E135.bottom", {"start": v(-216.4, -469.9) * mm, "end": v(673.6, -469.9) * mm});
            skLineSegment(sketch, "E135.top", {"start": v(-216.4, -508) * mm, "end": v(673.6, -508) * mm});
            skLineSegment(sketch, "E135.left", {"start": v(-216.4, -469.9) * mm, "end": v(-216.4, -508) * mm});
            skLineSegment(sketch, "E135.right", {"start": v(673.6, -469.9) * mm, "end": v(673.6, -508) * mm});
            skLineSegment(sketch, "E136.bottom", {"start": v(-171.45, -406.4) * mm, "end": v(-133.35, -406.4) * mm});
            skLineSegment(sketch, "E136.top", {"start": v(-171.45, -469.9) * mm, "end": v(-133.35, -469.9) * mm});
            skLineSegment(sketch, "E136.left", {"start": v(-171.45, -406.4) * mm, "end": v(-171.45, -469.9) * mm});
            skLineSegment(sketch, "E136.right", {"start": v(-133.35, -406.4) * mm, "end": v(-133.35, -469.9) * mm});
            skPoint(sketch, "E136.middle", {"position": v(-152.4, -438.15) * mm});
            skPoint(sketch, "E136.middle.positionSnap0", {"position": v(-216.4, -438.15) * mm});
            skPoint(sketch, "E136.centerSnap0", {"position": v(-216.4, -438.15) * mm});
            skPoint(sketch, "E137.1.0.0", {"position": v(-25.4, -438.15) * mm});
            skLineSegment(sketch, "E137.1.0.1", {"start": v(-6.35, -406.4) * mm, "end": v(-6.35, -469.9) * mm});
            skLineSegment(sketch, "E137.1.0.2", {"start": v(-44.45, -406.4) * mm, "end": v(-6.35, -406.4) * mm});
            skLineSegment(sketch, "E137.1.0.3", {"start": v(-44.45, -469.9) * mm, "end": v(-6.35, -469.9) * mm});
            skLineSegment(sketch, "E137.1.0.4", {"start": v(-44.45, -406.4) * mm, "end": v(-44.45, -469.9) * mm});
            skPoint(sketch, "E137.2.0.0", {"position": v(101.6, -438.15) * mm});
            skLineSegment(sketch, "E137.2.0.1", {"start": v(120.65, -406.4) * mm, "end": v(120.65, -469.9) * mm});
            skLineSegment(sketch, "E137.2.0.2", {"start": v(82.55, -406.4) * mm, "end": v(120.65, -406.4) * mm});
            skLineSegment(sketch, "E137.2.0.3", {"start": v(82.55, -469.9) * mm, "end": v(120.65, -469.9) * mm});
            skLineSegment(sketch, "E137.2.0.4", {"start": v(82.55, -406.4) * mm, "end": v(82.55, -469.9) * mm});
            skPoint(sketch, "E137.3.0.0", {"position": v(228.6, -438.15) * mm});
            skLineSegment(sketch, "E137.3.0.1", {"start": v(247.65, -406.4) * mm, "end": v(247.65, -469.9) * mm});
            skLineSegment(sketch, "E137.3.0.2", {"start": v(209.55, -406.4) * mm, "end": v(247.65, -406.4) * mm});
            skLineSegment(sketch, "E137.3.0.3", {"start": v(209.55, -469.9) * mm, "end": v(247.65, -469.9) * mm});
            skLineSegment(sketch, "E137.3.0.4", {"start": v(209.55, -406.4) * mm, "end": v(209.55, -469.9) * mm});
            skPoint(sketch, "E137.4.0.0", {"position": v(355.6, -438.15) * mm});
            skLineSegment(sketch, "E137.4.0.1", {"start": v(374.65, -406.4) * mm, "end": v(374.65, -469.9) * mm});
            skLineSegment(sketch, "E137.4.0.2", {"start": v(336.55, -406.4) * mm, "end": v(374.65, -406.4) * mm});
            skLineSegment(sketch, "E137.4.0.3", {"start": v(336.55, -469.9) * mm, "end": v(374.65, -469.9) * mm});
            skLineSegment(sketch, "E137.4.0.4", {"start": v(336.55, -406.4) * mm, "end": v(336.55, -469.9) * mm});
            skPoint(sketch, "E137.5.0.0", {"position": v(482.6, -438.15) * mm});
            skLineSegment(sketch, "E137.5.0.1", {"start": v(501.65, -406.4) * mm, "end": v(501.65, -469.9) * mm});
            skLineSegment(sketch, "E137.5.0.2", {"start": v(463.55, -406.4) * mm, "end": v(501.65, -406.4) * mm});
            skLineSegment(sketch, "E137.5.0.3", {"start": v(463.55, -469.9) * mm, "end": v(501.65, -469.9) * mm});
            skLineSegment(sketch, "E137.5.0.4", {"start": v(463.55, -406.4) * mm, "end": v(463.55, -469.9) * mm});
            skLineSegment(sketch, "E137.direction1", {"start": v(-152.4, -438.15) * mm, "end": v(-25.4, -438.15) * mm, "construction": true});
            skPoint(sketch, "E138.0.6.0", {"position": v(609.6, -438.15) * mm});
            skLineSegment(sketch, "E138.1.6.0", {"start": v(628.65, -406.4) * mm, "end": v(628.65, -469.9) * mm});
            skLineSegment(sketch, "E138.4.6.0", {"start": v(590.55, -406.4) * mm, "end": v(628.65, -406.4) * mm});
            skLineSegment(sketch, "E138.7.6.0", {"start": v(590.55, -469.9) * mm, "end": v(628.65, -469.9) * mm});
            skLineSegment(sketch, "E138.10.6.0", {"start": v(590.55, -406.4) * mm, "end": v(590.55, -469.9) * mm});
            skLineSegment(sketch, "E139.bottom", {"start": v(-171.45, -328.61) * mm, "end": v(-133.35, -328.61) * mm});
            skLineSegment(sketch, "E139.top", {"start": v(-171.45, -342.58) * mm, "end": v(-133.35, -342.58) * mm});
            skLineSegment(sketch, "E139.left", {"start": v(-171.45, -328.61) * mm, "end": v(-171.45, -342.58) * mm});
            skLineSegment(sketch, "E139.right", {"start": v(-133.35, -328.61) * mm, "end": v(-133.35, -342.58) * mm});
            skLineSegment(sketch, "E140.1.0.0", {"start": v(-44.45, -342.58) * mm, "end": v(-6.35, -342.58) * mm});
            skLineSegment(sketch, "E140.1.0.1", {"start": v(-44.45, -328.61) * mm, "end": v(-44.45, -342.58) * mm});
            skLineSegment(sketch, "E140.1.0.2", {"start": v(-6.35, -328.61) * mm, "end": v(-6.35, -342.58) * mm});
            skLineSegment(sketch, "E140.1.0.3", {"start": v(-44.45, -328.61) * mm, "end": v(-6.35, -328.61) * mm});
            skLineSegment(sketch, "E140.2.0.0", {"start": v(82.55, -342.58) * mm, "end": v(120.65, -342.58) * mm});
            skLineSegment(sketch, "E140.2.0.1", {"start": v(82.55, -328.61) * mm, "end": v(82.55, -342.58) * mm});
            skLineSegment(sketch, "E140.2.0.2", {"start": v(120.65, -328.61) * mm, "end": v(120.65, -342.58) * mm});
            skLineSegment(sketch, "E140.2.0.3", {"start": v(82.55, -328.61) * mm, "end": v(120.65, -328.61) * mm});
            skLineSegment(sketch, "E140.3.0.0", {"start": v(209.55, -342.58) * mm, "end": v(247.65, -342.58) * mm});
            skLineSegment(sketch, "E140.3.0.1", {"start": v(209.55, -328.61) * mm, "end": v(209.55, -342.58) * mm});
            skLineSegment(sketch, "E140.3.0.2", {"start": v(247.65, -328.61) * mm, "end": v(247.65, -342.58) * mm});
            skLineSegment(sketch, "E140.3.0.3", {"start": v(209.55, -328.61) * mm, "end": v(247.65, -328.61) * mm});
            skLineSegment(sketch, "E140.4.0.0", {"start": v(336.55, -342.58) * mm, "end": v(374.65, -342.58) * mm});
            skLineSegment(sketch, "E140.4.0.1", {"start": v(336.55, -328.61) * mm, "end": v(336.55, -342.58) * mm});
            skLineSegment(sketch, "E140.4.0.2", {"start": v(374.65, -328.61) * mm, "end": v(374.65, -342.58) * mm});
            skLineSegment(sketch, "E140.4.0.3", {"start": v(336.55, -328.61) * mm, "end": v(374.65, -328.61) * mm});
            skLineSegment(sketch, "E140.5.0.0", {"start": v(463.55, -342.58) * mm, "end": v(501.65, -342.58) * mm});
            skLineSegment(sketch, "E140.5.0.1", {"start": v(463.55, -328.61) * mm, "end": v(463.55, -342.58) * mm});
            skLineSegment(sketch, "E140.5.0.2", {"start": v(501.65, -328.61) * mm, "end": v(501.65, -342.58) * mm});
            skLineSegment(sketch, "E140.5.0.3", {"start": v(463.55, -328.61) * mm, "end": v(501.65, -328.61) * mm});
            skLineSegment(sketch, "E140.6.0.0", {"start": v(590.55, -342.58) * mm, "end": v(628.65, -342.58) * mm});
            skLineSegment(sketch, "E140.6.0.1", {"start": v(590.55, -328.61) * mm, "end": v(590.55, -342.58) * mm});
            skLineSegment(sketch, "E140.6.0.2", {"start": v(628.65, -328.61) * mm, "end": v(628.65, -342.58) * mm});
            skLineSegment(sketch, "E140.6.0.3", {"start": v(590.55, -328.61) * mm, "end": v(628.65, -328.61) * mm});
            skLineSegment(sketch, "E140.direction1", {"start": v(-171.45, -342.58) * mm, "end": v(-44.45, -342.58) * mm, "construction": true});
            skLineSegment(sketch, "E141", {"start": v(-952.5, -520.7) * mm, "end": v(-266.7, -520.7) * mm});
            skLineSegment(sketch, "E142.0", {"start": v(-952.5, -469.9) * mm, "end": v(-266.7, -469.9) * mm});
            skLineSegment(sketch, "E143", {"start": v(-1181.1, -393.7) * mm, "end": v(-952.5, -469.9) * mm});
            skLineSegment(sketch, "E144", {"start": v(-266.7, -520.7) * mm, "end": v(-266.7, -469.9) * mm});
            skLineSegment(sketch, "E145", {"start": v(-266.7, -495.3) * mm, "end": v(-1181.1, -495.3) * mm, "construction": true});
            skLineSegment(sketch, "E146.bottom", {"start": v(-1181.1, -457.2) * mm, "end": v(-1117.6, -457.2) * mm});
            skLineSegment(sketch, "E146.top", {"start": v(-1181.1, -469.4) * mm, "end": v(-1117.6, -469.4) * mm});
            skLineSegment(sketch, "E146.left", {"start": v(-1181.1, -457.2) * mm, "end": v(-1181.1, -469.4) * mm});
            skLineSegment(sketch, "E146.right", {"start": v(-1117.6, -457.2) * mm, "end": v(-1117.6, -469.4) * mm});
            skLineSegment(sketch, "E147.MirrorCS", {"start": v(-1181.1, -596.9) * mm, "end": v(-952.5, -520.7) * mm});
            skLineSegment(sketch, "E148.MirrorCS", {"start": v(-1117.6, -533.4) * mm, "end": v(-1117.6, -521.2) * mm});
            skLineSegment(sketch, "E149.MirrorCS", {"start": v(-1181.1, -533.4) * mm, "end": v(-1181.1, -521.2) * mm});
            skLineSegment(sketch, "E150.MirrorCS", {"start": v(-1181.1, -521.2) * mm, "end": v(-1117.6, -521.2) * mm});
            skLineSegment(sketch, "E151.MirrorCS", {"start": v(-1181.1, -533.4) * mm, "end": v(-1117.6, -533.4) * mm});
            skLineSegment(sketch, "E152", {"start": v(-1181.1, -393.7) * mm, "end": v(-1181.1, -596.9) * mm});
            skPoint(sketch, "E153.orphan", {"position": v(-1181.1, -520.7) * mm});
            skLineSegment(sketch, "E154", {"start": v(1181.1, 584.2) * mm, "end": v(1181.1, 279.4) * mm});
            skLineSegment(sketch, "E155", {"start": v(1181.1, 279.4) * mm, "end": v(1048.8, 431.8) * mm});
            skLineSegment(sketch, "E156", {"start": v(1048.8, 431.8) * mm, "end": v(1181.1, 584.2) * mm});
            skLineSegment(sketch, "E157", {"start": v(1054.1, 437.9) * mm, "end": v(1054.1, 425.7) * mm});
            skLineSegment(sketch, "E158.bottom", {"start": v(1054.1, 437.9) * mm, "end": v(1117.6, 437.9) * mm});
            skLineSegment(sketch, "E158.top", {"start": v(1054.1, 425.7) * mm, "end": v(1117.6, 425.7) * mm});
            skLineSegment(sketch, "E158.right", {"start": v(1117.6, 437.9) * mm, "end": v(1117.6, 425.7) * mm});
            skCircle(sketch, "E159", {"center": v(-469.9, -495.3) * mm, "radius": 3.3 * mm});
            skCircle(sketch, "E160", {"center": v(-736.6, -495.3) * mm, "radius": 3.3 * mm});
            skSolve(sketch);
        }
        {
            var Q0;
            Q0=makeQuery(id+"F1.imprint","IMPRINT",FACE,{"disambiguationData":[TD([[makeQuery(id+"F1.imprint","IMPRINT",EDGE,{"derivedFrom":sQuery(id+"F1.wireOp",EDGE,"E15.0.6.0")}),-1.0]])]});
            var Q1;
            Q1=makeQuery(id+"F1.imprint","IMPRINT",FACE,{"disambiguationData":[TD([[makeQuery(id+"F1.imprint","IMPRINT",EDGE,{"derivedFrom":sQuery(id+"F1.wireOp",EDGE,"E3")}),-1.0]])]});
            var Q2;
            Q2=makeQuery(id+"F1.imprint","IMPRINT",FACE,{"disambiguationData":[TD([[makeQuery(id+"F1.imprint","IMPRINT",EDGE,{"derivedFrom":sQuery(id+"F1.wireOp",EDGE,"E4.1.0.0")}),-1.0]])]});
            var Q3;
            Q3=makeQuery(id+"F1.imprint","IMPRINT",FACE,{"disambiguationData":[TD([[makeQuery(id+"F1.imprint","IMPRINT",EDGE,{"derivedFrom":sQuery(id+"F1.wireOp",EDGE,"E4.2.0.0")}),-1.0]])]});
            var Q4;
            Q4=makeQuery(id+"F1.imprint","IMPRINT",FACE,{"disambiguationData":[TD([[makeQuery(id+"F1.imprint","IMPRINT",EDGE,{"derivedFrom":sQuery(id+"F1.wireOp",EDGE,"E4.3.0.0")}),-1.0]])]});
            var Q5;
            Q5=makeQuery(id+"F1.imprint","IMPRINT",FACE,{"disambiguationData":[TD([[makeQuery(id+"F1.imprint","IMPRINT",EDGE,{"derivedFrom":sQuery(id+"F1.wireOp",EDGE,"E4.4.0.0")}),-1.0]])]});
            var Q6;
            Q6=makeQuery(id+"F1.imprint","IMPRINT",FACE,{"disambiguationData":[TD([[makeQuery(id+"F1.imprint","IMPRINT",EDGE,{"derivedFrom":sQuery(id+"F1.wireOp",EDGE,"E4.5.0.0")}),-1.0]])]});
            var Q7;
            Q7=makeQuery(id+"F1.imprint","IMPRINT",FACE,{"disambiguationData":[TD([[makeQuery(id+"F1.imprint","IMPRINT",EDGE,{"derivedFrom":sQuery(id+"F1.wireOp",EDGE,"E5")}),-1.0]])]});
            var Q8;
            Q8=makeQuery(id+"F1.imprint","IMPRINT",FACE,{"disambiguationData":[TD([[makeQuery(id+"F1.imprint","IMPRINT",EDGE,{"derivedFrom":sQuery(id+"F1.wireOp",EDGE,"E6.1.0.0")}),-1.0]])]});
            var Q9;
            Q9=makeQuery(id+"F1.imprint","IMPRINT",FACE,{"disambiguationData":[TD([[makeQuery(id+"F1.imprint","IMPRINT",EDGE,{"derivedFrom":sQuery(id+"F1.wireOp",EDGE,"E6.2.0.0")}),-1.0]])]});
            var Q10;
            Q10=makeQuery(id+"F1.imprint","IMPRINT",FACE,{"disambiguationData":[TD([[makeQuery(id+"F1.imprint","IMPRINT",EDGE,{"derivedFrom":sQuery(id+"F1.wireOp",EDGE,"E6.3.0.0")}),-1.0]])]});
            var Q11;
            Q11=makeQuery(id+"F1.imprint","IMPRINT",FACE,{"disambiguationData":[TD([[makeQuery(id+"F1.imprint","IMPRINT",EDGE,{"derivedFrom":sQuery(id+"F1.wireOp",EDGE,"E6.4.0.0")}),-1.0]])]});
            var Q12;
            Q12=makeQuery(id+"F1.imprint","IMPRINT",FACE,{"disambiguationData":[TD([[makeQuery(id+"F1.imprint","IMPRINT",EDGE,{"derivedFrom":sQuery(id+"F1.wireOp",EDGE,"E6.5.0.0")}),-1.0]])]});
            var Q13;
            {var subQ0=sQuery(id+"F1.wireOp",EDGE,"E18.0.5.0");Q13=makeQuery(id+"F1.imprint","IMPRINT",FACE,{"disambiguationData":[TD([[makeQuery(id+"F1.imprint","IMPRINT",EDGE,{"derivedFrom":subQ0}),1.0]])]});}
            var Q14;
            {var subQ0=sQuery(id+"F1.wireOp",EDGE,"E1.top");Q14=makeQuery(id+"F1.imprint","IMPRINT",FACE,{"disambiguationData":[TD([[makeQuery(id+"F1.imprint","IMPRINT",EDGE,{"derivedFrom":subQ0}),1.0]])]});}
            var Q15;
            {var subQ0=sQuery(id+"F1.wireOp",EDGE,"E2.top");Q15=makeQuery(id+"F1.imprint","IMPRINT",FACE,{"disambiguationData":[TD([[makeQuery(id+"F1.imprint","IMPRINT",EDGE,{"derivedFrom":subQ0}),1.0]])]});}
            var Q16;
            Q16=makeQuery(id+"F1.imprint","IMPRINT",FACE,{"disambiguationData":[TD([[makeQuery(id+"F1.imprint","IMPRINT",EDGE,{"derivedFrom":sQuery(id+"F1.wireOp",EDGE,"E64.bottom")}),-1.0]])]});
            var Q17;
            Q17=makeQuery(id+"F1.imprint","IMPRINT",FACE,{"disambiguationData":[TD([[makeQuery(id+"F1.imprint","IMPRINT",EDGE,{"derivedFrom":sQuery(id+"F1.wireOp",EDGE,"E73.bottom")}),-1.0]])]});
            var Q18;
            Q18=makeQuery(id+"F1.imprint","IMPRINT",FACE,{"disambiguationData":[TD([[makeQuery(id+"F1.imprint","IMPRINT",EDGE,{"derivedFrom":sQuery(id+"F1.wireOp",EDGE,"E98.MirrorC")}),1.0]])]});
            var Q19;
            Q19=makeQuery(id+"F1.imprint","IMPRINT",FACE,{"disambiguationData":[TD([[makeQuery(id+"F1.imprint","IMPRINT",EDGE,{"derivedFrom":sQuery(id+"F1.wireOp",EDGE,"E79.MirrorCS")}),1.0]])]});
            var Q20;
            {var subQ8=sQuery(id+"F1.wireOp",EDGE,"3cc9daea-cbba-44d1-9671-21d01c85290615.MirrorCS");Q20=makeQuery(id+"F1.imprint","IMPRINT",FACE,{"disambiguationData":[TD([[makeQuery(id+"F1.imprint","IMPRINT",EDGE,{"derivedFrom":subQ8}),-1.0]])]});}
            var Q21;
            Q21=makeQuery(id+"F1.imprint","IMPRINT",FACE,{"disambiguationData":[TD([[makeQuery(id+"F1.imprint","IMPRINT",EDGE,{"derivedFrom":sQuery(id+"F1.wireOp",EDGE,"3cc9daea-cbba-44d1-9671-21d01c85290657.MirrorCS")}),1.0]])]});
            var Q22;
            Q22=makeQuery(id+"F1.imprint","IMPRINT",FACE,{"disambiguationData":[TD([[makeQuery(id+"F1.imprint","IMPRINT",EDGE,{"derivedFrom":sQuery(id+"F1.wireOp",EDGE,"3cc9daea-cbba-44d1-9671-21d01c85290645.MirrorCS")}),1.0]])]});
            var Q23;
            Q23=makeQuery(id+"F1.imprint","IMPRINT",FACE,{"disambiguationData":[TD([[makeQuery(id+"F1.imprint","IMPRINT",EDGE,{"derivedFrom":sQuery(id+"F1.wireOp",EDGE,"3cc9daea-cbba-44d1-9671-21d01c85290633.MirrorC")}),1.0]])]});
            var Q24;
            Q24=makeQuery(id+"F1.imprint","IMPRINT",FACE,{"disambiguationData":[TD([[makeQuery(id+"F1.imprint","IMPRINT",EDGE,{"derivedFrom":sQuery(id+"F1.wireOp",EDGE,"3cc9daea-cbba-44d1-9671-21d01c85290625.MirrorCS")}),-1.0]])]});
            var Q25;
            {var subQ1=sQuery(id+"F1.wireOp",EDGE,"3cc9daea-cbba-44d1-9671-21d01c85290614.MirrorCS");Q25=makeQuery(id+"F1.imprint","IMPRINT",FACE,{"disambiguationData":[TD([[makeQuery(id+"F1.imprint","IMPRINT",EDGE,{"derivedFrom":subQ1}),1.0]])]});}
            var Q26;
            {var subQ1=sQuery(id+"F1.wireOp",EDGE,"3cc9daea-cbba-44d1-9671-21d01c85290616.MirrorCS");var subQ3=sQuery(id+"F1.wireOp",EDGE,"3cc9daea-cbba-44d1-9671-21d01c85290618.MirrorCS");var subQ4=makeQuery(id+"F1.imprint","INTERSECT",VERTEX,{"derivedFrom":[subQ1,subQ3]});Q26=makeQuery(id+"F1.imprint","IMPRINT",FACE,{"disambiguationData":[TD([[makeQuery(id+"F1.imprint","IMPRINT",EDGE,{"disambiguationData":[TD([[subQ4,-1.0]])],"derivedFrom":subQ3}),1.0]])]});}
            var Q27;
            {var subQ2=sQuery(id+"F1.wireOp",EDGE,"3cc9daea-cbba-44d1-9671-21d01c85290632.MirrorCS");Q27=makeQuery(id+"F1.imprint","IMPRINT",FACE,{"disambiguationData":[TD([[makeQuery(id+"F1.imprint","IMPRINT",EDGE,{"derivedFrom":subQ2}),-1.0]])]});}
            var Q28;
            {var subQ2=sQuery(id+"F1.wireOp",EDGE,"3cc9daea-cbba-44d1-9671-21d01c85290615.MirrorCS");Q28=makeQuery(id+"F1.imprint","IMPRINT",FACE,{"disambiguationData":[TD([[makeQuery(id+"F1.imprint","IMPRINT",EDGE,{"derivedFrom":subQ2}),1.0]])]});}
            var Q29;
            Q29=makeQuery(id+"F1.imprint","IMPRINT",FACE,{"disambiguationData":[TD([[makeQuery(id+"F1.imprint","IMPRINT",EDGE,{"derivedFrom":sQuery(id+"F1.wireOp",EDGE,"E87.MirrorCS")}),1.0]])]});
            var Q30;
            Q30=makeQuery(id+"F1.imprint","IMPRINT",FACE,{"disambiguationData":[TD([[makeQuery(id+"F1.imprint","IMPRINT",EDGE,{"derivedFrom":sQuery(id+"F1.wireOp",EDGE,"E85.MirrorCS")}),1.0]])]});
            var Q31;
            {var subQ1=sQuery(id+"F1.wireOp",EDGE,"E66.bottom");Q31=makeQuery(id+"F1.imprint","IMPRINT",FACE,{"disambiguationData":[TD([[makeQuery(id+"F1.imprint","IMPRINT",EDGE,{"derivedFrom":subQ1}),-1.0]])]});}
            var Q32;
            {var subQ1=sQuery(id+"F1.wireOp",EDGE,"E65.bottom");Q32=makeQuery(id+"F1.imprint","IMPRINT",FACE,{"disambiguationData":[TD([[makeQuery(id+"F1.imprint","IMPRINT",EDGE,{"derivedFrom":subQ1}),1.0]])]});}
            var Q33;
            {var subQ0=sQuery(id+"F1.wireOp",EDGE,"E64.top");Q33=makeQuery(id+"F1.imprint","IMPRINT",FACE,{"disambiguationData":[TD([[makeQuery(id+"F1.imprint","IMPRINT",EDGE,{"derivedFrom":subQ0}),1.0]])]});}
            var Q34;
            Q34=makeQuery(id+"F1.imprint","IMPRINT",FACE,{"disambiguationData":[TD([[makeQuery(id+"F1.imprint","IMPRINT",EDGE,{"derivedFrom":sQuery(id+"F1.wireOp",EDGE,"E67.bottom")}),-1.0]])]});
            var Q35;
            Q35=makeQuery(id+"F1.imprint","IMPRINT",FACE,{"disambiguationData":[TD([[makeQuery(id+"F1.imprint","IMPRINT",EDGE,{"derivedFrom":sQuery(id+"F1.wireOp",EDGE,"E68.bottom")}),1.0]])]});
            var Q36;
            Q36=makeQuery(id+"F1.imprint","IMPRINT",FACE,{"disambiguationData":[TD([[makeQuery(id+"F1.imprint","IMPRINT",EDGE,{"derivedFrom":sQuery(id+"F1.wireOp",EDGE,"E83.MirrorCS")}),-1.0]])]});
            var Q37;
            Q37=makeQuery(id+"F1.imprint","IMPRINT",FACE,{"disambiguationData":[TD([[makeQuery(id+"F1.imprint","IMPRINT",EDGE,{"derivedFrom":sQuery(id+"F1.wireOp",EDGE,"E81.MirrorCS")}),1.0]])]});
            var Q38;
            Q38=makeQuery(id+"F1.imprint","IMPRINT",FACE,{"disambiguationData":[TD([[makeQuery(id+"F1.imprint","IMPRINT",EDGE,{"derivedFrom":sQuery(id+"F1.wireOp",EDGE,"3cc9daea-cbba-44d1-9671-21d01c85290613.MirrorCS")}),1.0]])]});
            var Q39;
            Q39=makeQuery(id+"F1.imprint","IMPRINT",FACE,{"disambiguationData":[TD([[makeQuery(id+"F1.imprint","IMPRINT",EDGE,{"derivedFrom":sQuery(id+"F1.wireOp",EDGE,"3cc9daea-cbba-44d1-9671-21d01c85290642.MirrorCS")}),-1.0]])]});
            var Q40;
            Q40=makeQuery(id+"F1.imprint","IMPRINT",FACE,{"disambiguationData":[TD([[makeQuery(id+"F1.imprint","IMPRINT",EDGE,{"derivedFrom":sQuery(id+"F1.wireOp",EDGE,"3cc9daea-cbba-44d1-9671-21d01c85290620.MirrorCS")}),-1.0]])]});
            var Q41;
            Q41=makeQuery(id+"F1.imprint","IMPRINT",FACE,{"disambiguationData":[TD([[makeQuery(id+"F1.imprint","IMPRINT",EDGE,{"derivedFrom":sQuery(id+"F1.wireOp",EDGE,"3cc9daea-cbba-44d1-9671-21d01c85290621.MirrorCS")}),-1.0]])]});
            var Q42;
            Q42=makeQuery(id+"F1.imprint","IMPRINT",FACE,{"disambiguationData":[TD([[makeQuery(id+"F1.imprint","IMPRINT",EDGE,{"derivedFrom":sQuery(id+"F1.wireOp",EDGE,"E72.bottom")}),-1.0]])]});
            var Q43;
            {var subQ0=sQuery(id+"F1.wireOp",EDGE,"E89.MirrorCS");Q43=makeQuery(id+"F1.imprint","IMPRINT",FACE,{"disambiguationData":[TD([[makeQuery(id+"F1.imprint","IMPRINT",EDGE,{"derivedFrom":subQ0}),1.0]])]});}
            var Q44;
            {var subQ0=sQuery(id+"F1.wireOp",EDGE,"E84.MirrorCS");Q44=makeQuery(id+"F1.imprint","IMPRINT",FACE,{"disambiguationData":[TD([[makeQuery(id+"F1.imprint","IMPRINT",EDGE,{"derivedFrom":subQ0}),1.0]])]});}
            var Q45;
            {var subQ0=sQuery(id+"F1.wireOp",EDGE,"3cc9daea-cbba-44d1-9671-21d01c85290626.MirrorCS");Q45=makeQuery(id+"F1.imprint","IMPRINT",FACE,{"disambiguationData":[TD([[makeQuery(id+"F1.imprint","IMPRINT",EDGE,{"derivedFrom":subQ0}),-1.0]])]});}
            var Q46;
            {var subQ0=sQuery(id+"F1.wireOp",EDGE,"3cc9daea-cbba-44d1-9671-21d01c8529068.MirrorCS");Q46=makeQuery(id+"F1.imprint","IMPRINT",FACE,{"disambiguationData":[TD([[makeQuery(id+"F1.imprint","IMPRINT",EDGE,{"derivedFrom":subQ0}),1.0]])]});}
            var Q47;
            {var subQ0=sQuery(id+"F1.wireOp",EDGE,"3cc9daea-cbba-44d1-9671-21d01c85290640.MirrorCS");Q47=makeQuery(id+"F1.imprint","IMPRINT",FACE,{"disambiguationData":[TD([[makeQuery(id+"F1.imprint","IMPRINT",EDGE,{"derivedFrom":subQ0}),1.0]])]});}
            var Q48;
            {var subQ0=sQuery(id+"F1.wireOp",EDGE,"3cc9daea-cbba-44d1-9671-21d01c85290612.MirrorCS");Q48=makeQuery(id+"F1.imprint","IMPRINT",FACE,{"disambiguationData":[TD([[makeQuery(id+"F1.imprint","IMPRINT",EDGE,{"derivedFrom":subQ0}),-1.0]])]});}
            var Q49;
            Q49=makeQuery(id+"F1.imprint","IMPRINT",FACE,{"disambiguationData":[TD([[makeQuery(id+"F1.imprint","IMPRINT",EDGE,{"derivedFrom":sQuery(id+"F1.wireOp",EDGE,"E71.bottom")}),1.0]])]});
            var Q50;
            {var subQ5=sQuery(id+"F1.wireOp",EDGE,"E129.MirrorCS");Q50=makeQuery(id+"F1.imprint","IMPRINT",FACE,{"disambiguationData":[TD([[makeQuery(id+"F1.imprint","IMPRINT",EDGE,{"derivedFrom":subQ5}),1.0]])]});}
            var Q51;
            Q51=makeQuery(id+"F1.imprint","IMPRINT",FACE,{"disambiguationData":[TD([[makeQuery(id+"F1.imprint","IMPRINT",EDGE,{"derivedFrom":sQuery(id+"F1.wireOp",EDGE,"E136.bottom")}),-1.0]])]});
            var Q52;
            Q52=makeQuery(id+"F1.imprint","IMPRINT",FACE,{"disambiguationData":[TD([[makeQuery(id+"F1.imprint","IMPRINT",EDGE,{"derivedFrom":sQuery(id+"F1.wireOp",EDGE,"E135.top")}),1.0]])]});
            var Q53;
            Q53=makeQuery(id+"F1.imprint","IMPRINT",FACE,{"disambiguationData":[TD([[makeQuery(id+"F1.imprint","IMPRINT",EDGE,{"derivedFrom":sQuery(id+"F1.wireOp",EDGE,"E137.1.0.1")}),-1.0]])]});
            var Q54;
            Q54=makeQuery(id+"F1.imprint","IMPRINT",FACE,{"disambiguationData":[TD([[makeQuery(id+"F1.imprint","IMPRINT",EDGE,{"derivedFrom":sQuery(id+"F1.wireOp",EDGE,"E137.2.0.1")}),-1.0]])]});
            var Q55;
            Q55=makeQuery(id+"F1.imprint","IMPRINT",FACE,{"disambiguationData":[TD([[makeQuery(id+"F1.imprint","IMPRINT",EDGE,{"derivedFrom":sQuery(id+"F1.wireOp",EDGE,"E137.3.0.1")}),-1.0]])]});
            var Q56;
            Q56=makeQuery(id+"F1.imprint","IMPRINT",FACE,{"disambiguationData":[TD([[makeQuery(id+"F1.imprint","IMPRINT",EDGE,{"derivedFrom":sQuery(id+"F1.wireOp",EDGE,"E137.4.0.1")}),-1.0]])]});
            var Q57;
            Q57=makeQuery(id+"F1.imprint","IMPRINT",FACE,{"disambiguationData":[TD([[makeQuery(id+"F1.imprint","IMPRINT",EDGE,{"derivedFrom":sQuery(id+"F1.wireOp",EDGE,"E137.5.0.1")}),-1.0]])]});
            var Q58;
            Q58=makeQuery(id+"F1.imprint","IMPRINT",FACE,{"disambiguationData":[TD([[makeQuery(id+"F1.imprint","IMPRINT",EDGE,{"derivedFrom":sQuery(id+"F1.wireOp",EDGE,"E138.1.6.0")}),-1.0]])]});
            var Q59;
            {var subQ2=sQuery(id+"F1.wireOp",EDGE,"E154");Q59=makeQuery(id+"F1.imprint","IMPRINT",FACE,{"disambiguationData":[TD([[makeQuery(id+"F1.imprint","IMPRINT",EDGE,{"derivedFrom":subQ2}),-1.0]])]});}
            extrude(context, id + "F2", {"entities" : qUnion([Q0, Q1, Q2, Q3, Q4, Q5, Q6, Q7, Q8, Q9, Q10, Q11, Q12, Q13, Q14, Q15, Q16, Q17, Q18, Q19, Q20, Q21, Q22, Q23, Q24, Q25, Q26, Q27, Q28, Q29, Q30, Q31, Q32, Q33, Q34, Q35, Q36, Q37, Q38, Q39, Q40, Q41, Q42, Q43, Q44, Q45, Q46, Q47, Q48, Q49, Q50, Q51, Q52, Q53, Q54, Q55, Q56, Q57, Q58, Q59]), "depth" : (getVariable(context, 'Thickness')) * mm});
        }
        {
            var Q0;
            {var subQ7=sQuery(id+"F1.wireOp",EDGE,"E31.0");Q0=makeQuery(id+"F1.imprint","IMPRINT",FACE,{"disambiguationData":[TD([[makeQuery(id+"F1.imprint","IMPRINT",EDGE,{"derivedFrom":subQ7}),1.0]])]});}
            var Q1;
            {var subQ17=sQuery(id+"F1.wireOp",EDGE,"E33.0");Q1=makeQuery(id+"F1.imprint","IMPRINT",FACE,{"disambiguationData":[TD([[makeQuery(id+"F1.imprint","IMPRINT",EDGE,{"derivedFrom":subQ17}),1.0]])]});}
            extrude(context, id + "F3", {"entities" : qUnion([Q0, Q1]), "operationType" : NewBodyOperationType.ADD, "depth" : (getVariable(context, 'Thickness') / 2) * mm});
        }
        {
            var Q0;
            {var subQ0=sQuery(id+"F1.wireOp",EDGE,"E8.0");Q0=makeQuery(id+"F1.imprint","IMPRINT",FACE,{"disambiguationData":[TD([[makeQuery(id+"F1.imprint","IMPRINT",EDGE,{"derivedFrom":subQ0}),1.0]])]});}
            var Q1;
            {var subQ0=sQuery(id+"F1.wireOp",EDGE,"E10.1.0.0");Q1=makeQuery(id+"F1.imprint","IMPRINT",FACE,{"disambiguationData":[TD([[makeQuery(id+"F1.imprint","IMPRINT",EDGE,{"derivedFrom":subQ0}),-1.0]])]});}
            var Q2;
            {var subQ0=sQuery(id+"F1.wireOp",EDGE,"E10.2.0.0");Q2=makeQuery(id+"F1.imprint","IMPRINT",FACE,{"disambiguationData":[TD([[makeQuery(id+"F1.imprint","IMPRINT",EDGE,{"derivedFrom":subQ0}),-1.0]])]});}
            var Q3;
            {var subQ0=sQuery(id+"F1.wireOp",EDGE,"E10.3.0.0");Q3=makeQuery(id+"F1.imprint","IMPRINT",FACE,{"disambiguationData":[TD([[makeQuery(id+"F1.imprint","IMPRINT",EDGE,{"derivedFrom":subQ0}),-1.0]])]});}
            var Q4;
            {var subQ0=sQuery(id+"F1.wireOp",EDGE,"E10.4.0.0");Q4=makeQuery(id+"F1.imprint","IMPRINT",FACE,{"disambiguationData":[TD([[makeQuery(id+"F1.imprint","IMPRINT",EDGE,{"derivedFrom":subQ0}),-1.0]])]});}
            var Q5;
            {var subQ0=sQuery(id+"F1.wireOp",EDGE,"E17.0.5.0");Q5=makeQuery(id+"F1.imprint","IMPRINT",FACE,{"disambiguationData":[TD([[makeQuery(id+"F1.imprint","IMPRINT",EDGE,{"derivedFrom":subQ0}),-1.0]])]});}
            var Q6;
            {var subQ0=sQuery(id+"F1.wireOp",EDGE,"E12.0");Q6=makeQuery(id+"F1.imprint","IMPRINT",FACE,{"disambiguationData":[TD([[makeQuery(id+"F1.imprint","IMPRINT",EDGE,{"derivedFrom":subQ0}),-1.0]])]});}
            var Q7;
            {var subQ0=sQuery(id+"F1.wireOp",EDGE,"E14.1.0.0");Q7=makeQuery(id+"F1.imprint","IMPRINT",FACE,{"disambiguationData":[TD([[makeQuery(id+"F1.imprint","IMPRINT",EDGE,{"derivedFrom":subQ0}),-1.0]])]});}
            var Q8;
            {var subQ0=sQuery(id+"F1.wireOp",EDGE,"E14.2.0.0");Q8=makeQuery(id+"F1.imprint","IMPRINT",FACE,{"disambiguationData":[TD([[makeQuery(id+"F1.imprint","IMPRINT",EDGE,{"derivedFrom":subQ0}),-1.0]])]});}
            var Q9;
            {var subQ0=sQuery(id+"F1.wireOp",EDGE,"E14.3.0.0");Q9=makeQuery(id+"F1.imprint","IMPRINT",FACE,{"disambiguationData":[TD([[makeQuery(id+"F1.imprint","IMPRINT",EDGE,{"derivedFrom":subQ0}),-1.0]])]});}
            var Q10;
            {var subQ0=sQuery(id+"F1.wireOp",EDGE,"E14.4.0.0");Q10=makeQuery(id+"F1.imprint","IMPRINT",FACE,{"disambiguationData":[TD([[makeQuery(id+"F1.imprint","IMPRINT",EDGE,{"derivedFrom":subQ0}),-1.0]])]});}
            var Q11;
            {var subQ0=sQuery(id+"F1.wireOp",EDGE,"E18.0.5.0");Q11=makeQuery(id+"F1.imprint","IMPRINT",FACE,{"disambiguationData":[TD([[makeQuery(id+"F1.imprint","IMPRINT",EDGE,{"derivedFrom":subQ0}),-1.0]])]});}
            extrude(context, id + "F4", {"entities" : qUnion([Q0, Q1, Q2, Q3, Q4, Q5, Q6, Q7, Q8, Q9, Q10, Q11]), "operationType" : NewBodyOperationType.ADD, "depth" : (getVariable(context, 'Thickness') / 2) * mm});
        }
        {
            var Q0;
            Q0=makeQuery(id+"F1.imprint","IMPRINT",FACE,{"disambiguationData":[TD([[makeQuery(id+"F1.imprint","IMPRINT",EDGE,{"derivedFrom":sQuery(id+"F1.wireOp",EDGE,"E141")}),1.0]])]});
            extrude(context, id + "F5", {"entities" : qUnion([Q0]), "depth" : 18.03 * mm});
        }
    });
